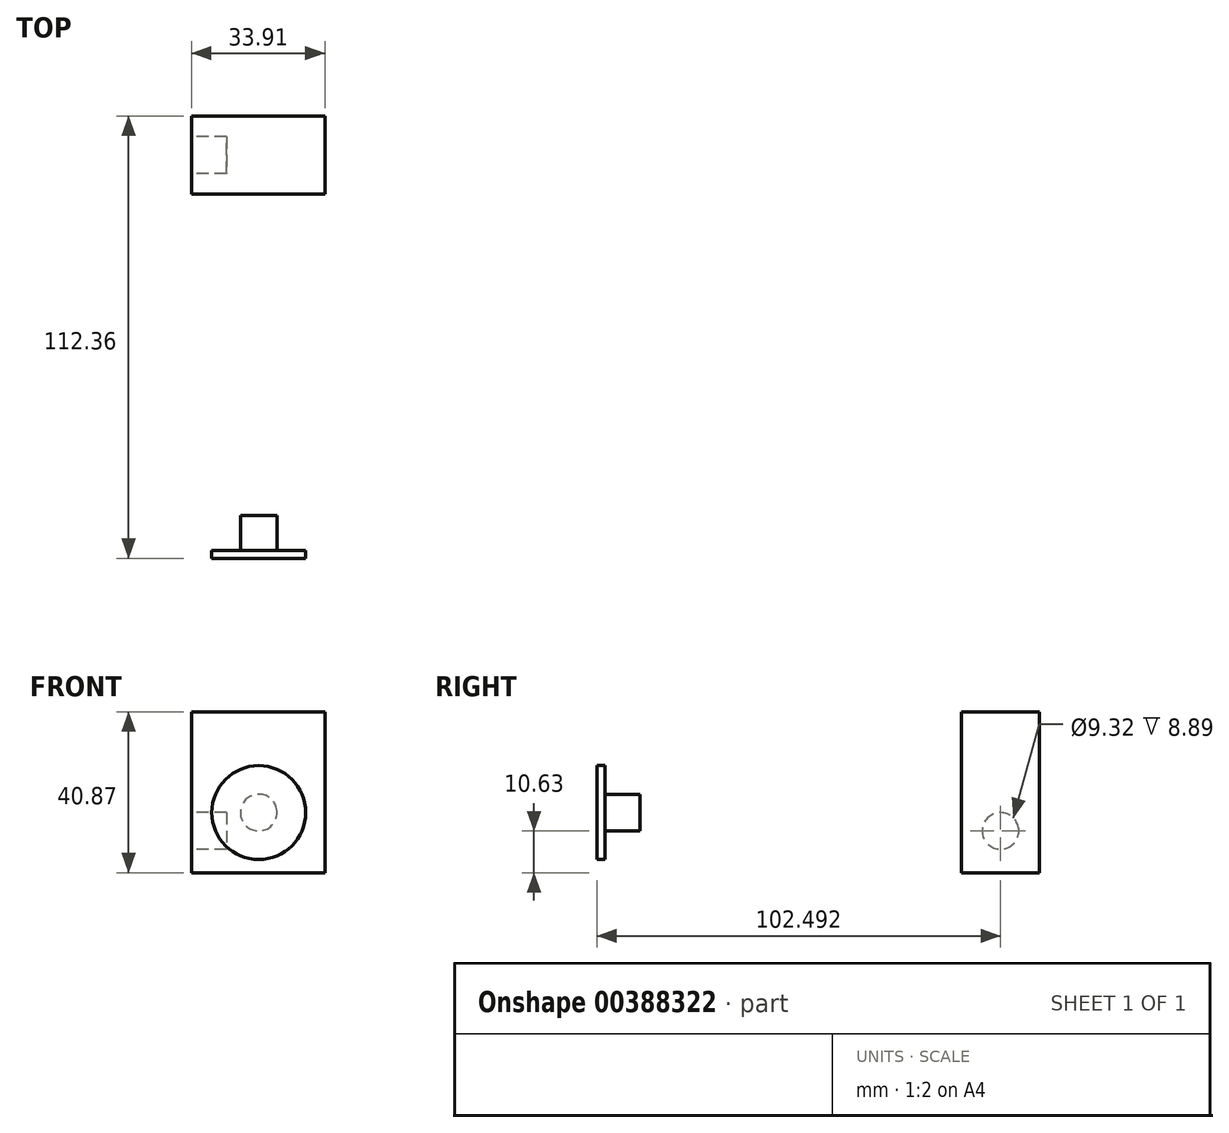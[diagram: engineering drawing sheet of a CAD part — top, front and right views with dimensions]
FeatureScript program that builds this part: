
annotation { "Feature Type Name" : "Feature", "Feature Type Description" : "" }
export const myFeature = defineFeature(function(context is Context, id is Id, definition is map)
    precondition{}
    {
        {
            var Q0;
            Q0=qCreatedBy(makeId("Front.planeOp"),FACE);
            var sketch = newSketch(context, id + "F0", { "sketchPlane" : qUnion([Q0])});
            skLineSegment(sketch, "E0", {"start": v(-17.1, 30.24) * mm, "end": v(-17.1, -10.63) * mm});
            skLineSegment(sketch, "E1", {"start": v(-17.1, -10.63) * mm, "end": v(16.82, -10.63) * mm});
            skLineSegment(sketch, "E2", {"start": v(16.82, -10.63) * mm, "end": v(16.82, 30.24) * mm});
            skLineSegment(sketch, "E3", {"start": v(-17.1, 30.24) * mm, "end": v(16.82, 30.24) * mm});
            skSolve(sketch);
        }
        {
            var Q0;
            Q0=qSketchRegion(id+"F0",true);
            extrude(context, id + "F1", {"entities" : qUnion([Q0]), "depth" : 19.74 * mm});
        }
        {
            var Q0;
            Q0=makeQuery(id+"F1.opExtrude","SWEPT_FACE",FACE,{"disambiguationData":[OSD([sQuery(id+"F0.wireOp",EDGE,"E0")])]});
            var sketch = newSketch(context, id + "F2", { "sketchPlane" : qUnion([Q0])});
            skCircle(sketch, "E4", {"center": v(9.87, 0) * mm, "radius": 4.66 * mm});
            skPoint(sketch, "E4.centerSnap0", {"position": v(9.87, -10.63) * mm});
            skSolve(sketch);
        }
        {
            var Q0;
            Q0=qSketchRegion(id+"F2",true);
            extrude(context, id + "F3", {"entities" : qUnion([Q0]), "operationType" : NewBodyOperationType.REMOVE, "oppositeDirection" : true, "depth" : 8.9 * mm});
        }
        {
            var Q0;
            Q0=makeQuery(id+"F1.opExtrude","CAP_FACE",FACE,{"disambiguationData":[OSD([sQuery(id+"F0.wireOp",EDGE,"E0"),sQuery(id+"F0.wireOp",EDGE,"E1"),sQuery(id+"F0.wireOp",EDGE,"E2"),sQuery(id+"F0.wireOp",EDGE,"E3")])],"isStart":false});
            cPlane(context, id + "F4", {"entities" : qUnion([Q0]), "cplaneType" : CPlaneType.OFFSET, "offset" : 81.7 * mm, "width" : 152.4 * mm, "height" : 152.4 * mm});
        }
        {
            var Q0;
            Q0=qCreatedBy(id+"F4.planeOp",FACE);
            var sketch = newSketch(context, id + "F5", { "sketchPlane" : qUnion([Q0])});
            skCircle(sketch, "E5", {"center": v(0, 4.66) * mm, "radius": 4.66 * mm});
            skSolve(sketch);
        }
        {
            var Q0;
            Q0=qSketchRegion(id+"F5",true);
            extrude(context, id + "F6", {"entities" : qUnion([Q0]), "depth" : 8.9 * mm});
        }
        {
            var Q0;
            Q0=makeQuery(id+"F6.opExtrude","CAP_FACE",FACE,{"disambiguationData":[OSD([sQuery(id+"F5.wireOp",EDGE,"E5")])],"isStart":false});
            var sketch = newSketch(context, id + "F7", { "sketchPlane" : qUnion([Q0])});
            skLineSegment(sketch, "E6", {"start": v(0, 0) * mm, "end": v(0, 9.32) * mm, "construction": true});
            skCircle(sketch, "E7", {"center": v(0, 4.66) * mm, "radius": 11.94 * mm});
            skSolve(sketch);
        }
        {
            var Q0;
            Q0=qSketchRegion(id+"F7",true);
            extrude(context, id + "F8", {"entities" : qUnion([Q0]), "operationType" : NewBodyOperationType.ADD, "depth" : 2.03 * mm});
        }
    });
